# Revit family: RN 55035 Optipress-Therm-Übergang
name_source: partatom
category: Rohrformteile
units: mm (PartAtom-declared; Revit-internal decimal feet)

## family parameters
Arbeitsebenenbasiert = Nein
Beim Laden mit Abzugskörper schneiden = Nein
Bemaßung runder Anschluss = Durchmesser verwenden
Gemeinsam genutzt = Nein
Immer vertikal = Ja
Teiletyp = Verbindung

## types (23) — shared parameters
1.010.00.2 Blattnummer der Richtlinie = 29
1.010.00.3 Ausgabedatum (Monat) der Richtlinie = 201308
1.010.00.4 Herstellername = R. Nussbaum AG
1.010.00.5 Revisionsdatum der Datei = 20190521
1.010.00.6 Webadresse des Herstellers = http://www.nussbaum.ch
1.100.00.4 Produktbezeichnung = Versorgung
1.110.00.2 Index = 1
1.110.00.4 Produktbezeichnung = Optipress-Therm
1.960/3L.00.8 Link (URL) = https://www.nussbaum.ch
29.700.00.4 Produktname = Optipress-Therm-Übergang, mit Aussengewinde
29.700.00.5 Produktkennung = 2
29.700.00.6 Querschnittsform = 1
29.700.00.7 Nennweitensystem = DN
29.700.00.8 Nenndrucksystem = PN
29.710.02.4 Nenndruck = 16
29.710.02.5 max. zul. Überdruck [hPa] = 1600
29.710.02.7 max. zul. Dauer-Betriebsdruck [hPa] = 1600
29.710.02.9 max. zul. Dauer-Betriebstemperatur [°C] = 95
Connector Visibility = Nein
EnclosingSpace Visibility = Nein
R. Nussbaum AG 55035.30 de Visibility = Nein

## per-type parameters (varying)
- DN=60x65: 1.800.00.3 TGA-Nummer=01900100000000000000000000000000000000000000000022000000000000000023; 1.800.00.4 Kommentarfeld=55035.70, Optipress-Therm-Übergang, mit Aussengewinde, DN=60x65, L=108, R=2½; 1.810.00.3 Hersteller-Bestellnummer=55035.70; 1.810.00.4 DATANORM-Nummer=55035.70; 1.810.00.5 StLB-Nummer=255.624; 1.810.00.6 GTIN-Nummer=7612945679499; 29.710.02.10 Formstück-Gewicht [kg]=0.955; 29.710.02.3 Benennung=Optipress-Therm-Übergang, mit Aussengewinde, DN=60x65, L=108, R=2½; CONNECTOR0_DIAMETER_dX_0r=60 mm; CONNECTOR0_dX_01=43 mm  [stored 0.141076 ft]; CONNECTOR0_ref_dX=43 mm  [stored 0.141076 ft]; CONNECTOR1_DIAMETER_dX_0r=65 mm; CONNECTOR1_dX_00=81 mm; CONNECTOR1_dX_01=108 mm  [stored 0.354331 ft]; CONNECTOR1_ref_dX=81 mm; CONNENCTOR1_ref1_02=108 mm  [stored 0.354331 ft]; R. Nussbaum AG 55035.21 de Visibility=Nein; R. Nussbaum AG 55035.22 de Visibility=Nein; R. Nussbaum AG 55035.23 de Visibility=Nein; R. Nussbaum AG 55035.24 de Visibility=Nein; R. Nussbaum AG 55035.25 de Visibility=Nein; R. Nussbaum AG 55035.26 de Visibility=Nein; R. Nussbaum AG 55035.27 de Visibility=Nein; R. Nussbaum AG 55035.28 de Visibility=Nein; R. Nussbaum AG 55035.29 de Visibility=Nein; R. Nussbaum AG 55035.31 de Visibility=Nein; R. Nussbaum AG 55035.32 de Visibility=Nein; R. Nussbaum AG 55035.33 de Visibility=Nein; R. Nussbaum AG 55035.34 de Visibility=Nein; R. Nussbaum AG 55035.35 de Visibility=Nein; R. Nussbaum AG 55035.36 de Visibility=Nein; R. Nussbaum AG 55035.37 de Visibility=Nein; R. Nussbaum AG 55035.38 de Visibility=Nein; R. Nussbaum AG 55035.69 de Visibility=Nein; R. Nussbaum AG 55035.70 de Visibility=Ja; R. Nussbaum AG 55035.71 de Visibility=Nein; R. Nussbaum AG 55035.72 de Visibility=Nein; R. Nussbaum AG 55035.73 de Visibility=Nein
- DN=15x20: 1.800.00.3 TGA-Nummer=01900100000000000000000000000000000000000000000022000000000000000004; 1.800.00.4 Kommentarfeld=55035.24, Optipress-Therm-Übergang, mit Aussengewinde, DN=15x20, L=49, R=¾; 1.810.00.3 Hersteller-Bestellnummer=55035.24; 1.810.00.4 DATANORM-Nummer=55035.24; 1.810.00.5 StLB-Nummer=255.613; 1.810.00.6 GTIN-Nummer=7612945662378; 29.710.02.10 Formstück-Gewicht [kg]=0.059; 29.710.02.3 Benennung=Optipress-Therm-Übergang, mit Aussengewinde, DN=15x20, L=49, R=¾; CONNECTOR0_DIAMETER_dX_0r=15 mm  [stored 0.0492126 ft]; CONNECTOR0_dX_01=22 mm; CONNECTOR0_ref_dX=22 mm; CONNECTOR1_DIAMETER_dX_0r=20 mm; CONNECTOR1_dX_00=34 mm; CONNECTOR1_dX_01=49 mm; CONNECTOR1_ref_dX=34 mm; CONNENCTOR1_ref1_02=49 mm; R. Nussbaum AG 55035.21 de Visibility=Nein; R. Nussbaum AG 55035.22 de Visibility=Nein; R. Nussbaum AG 55035.23 de Visibility=Nein; R. Nussbaum AG 55035.24 de Visibility=Ja; R. Nussbaum AG 55035.25 de Visibility=Nein; R. Nussbaum AG 55035.26 de Visibility=Nein; R. Nussbaum AG 55035.27 de Visibility=Nein; R. Nussbaum AG 55035.28 de Visibility=Nein; R. Nussbaum AG 55035.29 de Visibility=Nein; R. Nussbaum AG 55035.31 de Visibility=Nein; R. Nussbaum AG 55035.32 de Visibility=Nein; R. Nussbaum AG 55035.33 de Visibility=Nein; R. Nussbaum AG 55035.34 de Visibility=Nein; R. Nussbaum AG 55035.35 de Visibility=Nein; R. Nussbaum AG 55035.36 de Visibility=Nein; R. Nussbaum AG 55035.37 de Visibility=Nein; R. Nussbaum AG 55035.38 de Visibility=Nein; R. Nussbaum AG 55035.69 de Visibility=Nein; R. Nussbaum AG 55035.70 de Visibility=Nein; R. Nussbaum AG 55035.71 de Visibility=Nein; R. Nussbaum AG 55035.72 de Visibility=Nein; R. Nussbaum AG 55035.73 de Visibility=Nein
- DN=100: 1.800.00.3 TGA-Nummer=01900100000000000000000000000000000000000000000022000000000000000021; 1.800.00.4 Kommentarfeld=55035.73, Optipress-Therm-Übergang, mit Aussengewinde, DN=100, L=134, R=4; 1.810.00.3 Hersteller-Bestellnummer=55035.73; 1.810.00.4 DATANORM-Nummer=55035.73; 1.810.00.5 StLB-Nummer=255.623; 1.810.00.6 GTIN-Nummer=7612945699244; 29.710.02.10 Formstück-Gewicht [kg]=1.553; 29.710.02.3 Benennung=Optipress-Therm-Übergang, mit Aussengewinde, DN=100, L=134, R=4; CONNECTOR0_DIAMETER_dX_0r=100 mm  [stored 0.328084 ft]; CONNECTOR0_dX_01=60 mm; CONNECTOR0_ref_dX=60 mm; CONNECTOR1_DIAMETER_dX_0r=100 mm  [stored 0.328084 ft]; CONNECTOR1_dX_00=98 mm; CONNECTOR1_dX_01=134 mm; CONNECTOR1_ref_dX=98 mm; CONNENCTOR1_ref1_02=134 mm; R. Nussbaum AG 55035.21 de Visibility=Nein; R. Nussbaum AG 55035.22 de Visibility=Nein; R. Nussbaum AG 55035.23 de Visibility=Nein; R. Nussbaum AG 55035.24 de Visibility=Nein; R. Nussbaum AG 55035.25 de Visibility=Nein; R. Nussbaum AG 55035.26 de Visibility=Nein; R. Nussbaum AG 55035.27 de Visibility=Nein; R. Nussbaum AG 55035.28 de Visibility=Nein; R. Nussbaum AG 55035.29 de Visibility=Nein; R. Nussbaum AG 55035.31 de Visibility=Nein; R. Nussbaum AG 55035.32 de Visibility=Nein; R. Nussbaum AG 55035.33 de Visibility=Nein; R. Nussbaum AG 55035.34 de Visibility=Nein; R. Nussbaum AG 55035.35 de Visibility=Nein; R. Nussbaum AG 55035.36 de Visibility=Nein; R. Nussbaum AG 55035.37 de Visibility=Nein; R. Nussbaum AG 55035.38 de Visibility=Nein; R. Nussbaum AG 55035.69 de Visibility=Nein; R. Nussbaum AG 55035.70 de Visibility=Nein; R. Nussbaum AG 55035.71 de Visibility=Nein; R. Nussbaum AG 55035.72 de Visibility=Nein; R. Nussbaum AG 55035.73 de Visibility=Ja
- DN=80: 1.800.00.3 TGA-Nummer=01900100000000000000000000000000000000000000000022000000000000000020; 1.800.00.4 Kommentarfeld=55035.72, Optipress-Therm-Übergang, mit Aussengewinde, DN=80, L=118, R=3; 1.810.00.3 Hersteller-Bestellnummer=55035.72; 1.810.00.4 DATANORM-Nummer=55035.72; 1.810.00.5 StLB-Nummer=255.622; 1.810.00.6 GTIN-Nummer=7612945699237; 29.710.02.10 Formstück-Gewicht [kg]=1.023; 29.710.02.3 Benennung=Optipress-Therm-Übergang, mit Aussengewinde, DN=80, L=118, R=3; CONNECTOR0_DIAMETER_dX_0r=80 mm; CONNECTOR0_dX_01=50 mm; CONNECTOR0_ref_dX=50 mm; CONNECTOR1_DIAMETER_dX_0r=80 mm; CONNECTOR1_dX_00=88 mm; CONNECTOR1_dX_01=118 mm; CONNECTOR1_ref_dX=88 mm; CONNENCTOR1_ref1_02=118 mm; R. Nussbaum AG 55035.21 de Visibility=Nein; R. Nussbaum AG 55035.22 de Visibility=Nein; R. Nussbaum AG 55035.23 de Visibility=Nein; R. Nussbaum AG 55035.24 de Visibility=Nein; R. Nussbaum AG 55035.25 de Visibility=Nein; R. Nussbaum AG 55035.26 de Visibility=Nein; R. Nussbaum AG 55035.27 de Visibility=Nein; R. Nussbaum AG 55035.28 de Visibility=Nein; R. Nussbaum AG 55035.29 de Visibility=Nein; R. Nussbaum AG 55035.31 de Visibility=Nein; R. Nussbaum AG 55035.32 de Visibility=Nein; R. Nussbaum AG 55035.33 de Visibility=Nein; R. Nussbaum AG 55035.34 de Visibility=Nein; R. Nussbaum AG 55035.35 de Visibility=Nein; R. Nussbaum AG 55035.36 de Visibility=Nein; R. Nussbaum AG 55035.37 de Visibility=Nein; R. Nussbaum AG 55035.38 de Visibility=Nein; R. Nussbaum AG 55035.69 de Visibility=Nein; R. Nussbaum AG 55035.70 de Visibility=Nein; R. Nussbaum AG 55035.71 de Visibility=Nein; R. Nussbaum AG 55035.72 de Visibility=Ja; R. Nussbaum AG 55035.73 de Visibility=Nein
- DN=65: 1.800.00.3 TGA-Nummer=01900100000000000000000000000000000000000000000022000000000000000019; 1.800.00.4 Kommentarfeld=55035.71, Optipress-Therm-Übergang, mit Aussengewinde, DN=65, L=114, R=2½; 1.810.00.3 Hersteller-Bestellnummer=55035.71; 1.810.00.4 DATANORM-Nummer=55035.71; 1.810.00.5 StLB-Nummer=255.621; 1.810.00.6 GTIN-Nummer=7612945681003; 29.710.02.10 Formstück-Gewicht [kg]=0.868; 29.710.02.3 Benennung=Optipress-Therm-Übergang, mit Aussengewinde, DN=65, L=114, R=2½; CONNECTOR0_DIAMETER_dX_0r=65 mm; CONNECTOR0_dX_01=50 mm; CONNECTOR0_ref_dX=50 mm; CONNECTOR1_DIAMETER_dX_0r=65 mm; CONNECTOR1_dX_00=87 mm; CONNECTOR1_dX_01=114 mm; CONNECTOR1_ref_dX=87 mm; CONNENCTOR1_ref1_02=114 mm; R. Nussbaum AG 55035.21 de Visibility=Nein; R. Nussbaum AG 55035.22 de Visibility=Nein; R. Nussbaum AG 55035.23 de Visibility=Nein; R. Nussbaum AG 55035.24 de Visibility=Nein; R. Nussbaum AG 55035.25 de Visibility=Nein; R. Nussbaum AG 55035.26 de Visibility=Nein; R. Nussbaum AG 55035.27 de Visibility=Nein; R. Nussbaum AG 55035.28 de Visibility=Nein; R. Nussbaum AG 55035.29 de Visibility=Nein; R. Nussbaum AG 55035.31 de Visibility=Nein; R. Nussbaum AG 55035.32 de Visibility=Nein; R. Nussbaum AG 55035.33 de Visibility=Nein; R. Nussbaum AG 55035.34 de Visibility=Nein; R. Nussbaum AG 55035.35 de Visibility=Nein; R. Nussbaum AG 55035.36 de Visibility=Nein; R. Nussbaum AG 55035.37 de Visibility=Nein; R. Nussbaum AG 55035.38 de Visibility=Nein; R. Nussbaum AG 55035.69 de Visibility=Nein; R. Nussbaum AG 55035.70 de Visibility=Nein; R. Nussbaum AG 55035.71 de Visibility=Ja; R. Nussbaum AG 55035.72 de Visibility=Nein; R. Nussbaum AG 55035.73 de Visibility=Nein
- DN=60x50: 1.800.00.3 TGA-Nummer=01900100000000000000000000000000000000000000000022000000000000000018; 1.800.00.4 Kommentarfeld=55035.69, Optipress-Therm-Übergang, mit Aussengewinde, DN=60x50, L=97, R=2; 1.810.00.3 Hersteller-Bestellnummer=55035.69; 1.810.00.4 DATANORM-Nummer=55035.69; 1.810.00.5 StLB-Nummer=255.624; 1.810.00.6 GTIN-Nummer=7612945679482; 29.710.02.10 Formstück-Gewicht [kg]=0.453; 29.710.02.3 Benennung=Optipress-Therm-Übergang, mit Aussengewinde, DN=60x50, L=97, R=2; CONNECTOR0_DIAMETER_dX_0r=60 mm; CONNECTOR0_dX_01=43 mm  [stored 0.141076 ft]; CONNECTOR0_ref_dX=43 mm  [stored 0.141076 ft]; CONNECTOR1_DIAMETER_dX_0r=50 mm; CONNECTOR1_dX_00=73 mm; CONNECTOR1_dX_01=97 mm; CONNECTOR1_ref_dX=73 mm; CONNENCTOR1_ref1_02=97 mm; R. Nussbaum AG 55035.21 de Visibility=Nein; R. Nussbaum AG 55035.22 de Visibility=Nein; R. Nussbaum AG 55035.23 de Visibility=Nein; R. Nussbaum AG 55035.24 de Visibility=Nein; R. Nussbaum AG 55035.25 de Visibility=Nein; R. Nussbaum AG 55035.26 de Visibility=Nein; R. Nussbaum AG 55035.27 de Visibility=Nein; R. Nussbaum AG 55035.28 de Visibility=Nein; R. Nussbaum AG 55035.29 de Visibility=Nein; R. Nussbaum AG 55035.31 de Visibility=Nein; R. Nussbaum AG 55035.32 de Visibility=Nein; R. Nussbaum AG 55035.33 de Visibility=Nein; R. Nussbaum AG 55035.34 de Visibility=Nein; R. Nussbaum AG 55035.35 de Visibility=Nein; R. Nussbaum AG 55035.36 de Visibility=Nein; R. Nussbaum AG 55035.37 de Visibility=Nein; R. Nussbaum AG 55035.38 de Visibility=Nein; R. Nussbaum AG 55035.69 de Visibility=Ja; R. Nussbaum AG 55035.70 de Visibility=Nein; R. Nussbaum AG 55035.71 de Visibility=Nein; R. Nussbaum AG 55035.72 de Visibility=Nein; R. Nussbaum AG 55035.73 de Visibility=Nein
- DN=25x15: 1.800.00.3 TGA-Nummer=01900100000000000000000000000000000000000000000022000000000000000017; 1.800.00.4 Kommentarfeld=55035.38, Optipress-Therm-Übergang, mit Aussengewinde, DN=25x15, L=50, R=½; 1.810.00.3 Hersteller-Bestellnummer=55035.38; 1.810.00.4 DATANORM-Nummer=55035.38; 1.810.00.5 StLB-Nummer=255.615; 1.810.00.6 GTIN-Nummer=7612945716378; 29.710.02.10 Formstück-Gewicht [kg]=0.088; 29.710.02.3 Benennung=Optipress-Therm-Übergang, mit Aussengewinde, DN=25x15, L=50, R=½; CONNECTOR0_DIAMETER_dX_0r=25 mm  [stored 0.082021 ft]; CONNECTOR0_dX_01=24 mm; CONNECTOR0_ref_dX=24 mm; CONNECTOR1_DIAMETER_dX_0r=15 mm  [stored 0.0492126 ft]; CONNECTOR1_dX_00=37 mm; CONNECTOR1_dX_01=50 mm; CONNECTOR1_ref_dX=37 mm; CONNENCTOR1_ref1_02=50 mm; R. Nussbaum AG 55035.21 de Visibility=Nein; R. Nussbaum AG 55035.22 de Visibility=Nein; R. Nussbaum AG 55035.23 de Visibility=Nein; R. Nussbaum AG 55035.24 de Visibility=Nein; R. Nussbaum AG 55035.25 de Visibility=Nein; R. Nussbaum AG 55035.26 de Visibility=Nein; R. Nussbaum AG 55035.27 de Visibility=Nein; R. Nussbaum AG 55035.28 de Visibility=Nein; R. Nussbaum AG 55035.29 de Visibility=Nein; R. Nussbaum AG 55035.31 de Visibility=Nein; R. Nussbaum AG 55035.32 de Visibility=Nein; R. Nussbaum AG 55035.33 de Visibility=Nein; R. Nussbaum AG 55035.34 de Visibility=Nein; R. Nussbaum AG 55035.35 de Visibility=Nein; R. Nussbaum AG 55035.36 de Visibility=Nein; R. Nussbaum AG 55035.37 de Visibility=Nein; R. Nussbaum AG 55035.38 de Visibility=Ja; R. Nussbaum AG 55035.69 de Visibility=Nein; R. Nussbaum AG 55035.70 de Visibility=Nein; R. Nussbaum AG 55035.71 de Visibility=Nein; R. Nussbaum AG 55035.72 de Visibility=Nein; R. Nussbaum AG 55035.73 de Visibility=Nein
- DN=40x32: 1.800.00.3 TGA-Nummer=01900100000000000000000000000000000000000000000022000000000000000016; 1.800.00.4 Kommentarfeld=55035.37, Optipress-Therm-Übergang, mit Aussengewinde, DN=40x32, L=77, R=1¼; 1.810.00.3 Hersteller-Bestellnummer=55035.37; 1.810.00.4 DATANORM-Nummer=55035.37; 1.810.00.5 StLB-Nummer=255.617; 1.810.00.6 GTIN-Nummer=7612945709004; 29.710.02.10 Formstück-Gewicht [kg]=0.334; 29.710.02.3 Benennung=Optipress-Therm-Übergang, mit Aussengewinde, DN=40x32, L=77, R=1¼; CONNECTOR0_DIAMETER_dX_0r=40 mm; CONNECTOR0_dX_01=36 mm; CONNECTOR0_ref_dX=36 mm; CONNECTOR1_DIAMETER_dX_0r=32 mm; CONNECTOR1_dX_00=58 mm; CONNECTOR1_dX_01=77 mm  [stored 0.252625 ft]; CONNECTOR1_ref_dX=58 mm; CONNENCTOR1_ref1_02=77 mm  [stored 0.252625 ft]; R. Nussbaum AG 55035.21 de Visibility=Nein; R. Nussbaum AG 55035.22 de Visibility=Nein; R. Nussbaum AG 55035.23 de Visibility=Nein; R. Nussbaum AG 55035.24 de Visibility=Nein; R. Nussbaum AG 55035.25 de Visibility=Nein; R. Nussbaum AG 55035.26 de Visibility=Nein; R. Nussbaum AG 55035.27 de Visibility=Nein; R. Nussbaum AG 55035.28 de Visibility=Nein; R. Nussbaum AG 55035.29 de Visibility=Nein; R. Nussbaum AG 55035.31 de Visibility=Nein; R. Nussbaum AG 55035.32 de Visibility=Nein; R. Nussbaum AG 55035.33 de Visibility=Nein; R. Nussbaum AG 55035.34 de Visibility=Nein; R. Nussbaum AG 55035.35 de Visibility=Nein; R. Nussbaum AG 55035.36 de Visibility=Nein; R. Nussbaum AG 55035.37 de Visibility=Ja; R. Nussbaum AG 55035.38 de Visibility=Nein; R. Nussbaum AG 55035.69 de Visibility=Nein; R. Nussbaum AG 55035.70 de Visibility=Nein; R. Nussbaum AG 55035.71 de Visibility=Nein; R. Nussbaum AG 55035.72 de Visibility=Nein; R. Nussbaum AG 55035.73 de Visibility=Nein
- DN=32x25: 1.800.00.3 TGA-Nummer=01900100000000000000000000000000000000000000000022000000000000000015; 1.800.00.4 Kommentarfeld=55035.36, Optipress-Therm-Übergang, mit Aussengewinde, DN=32x25, L=60, R=1; 1.810.00.3 Hersteller-Bestellnummer=55035.36; 1.810.00.4 DATANORM-Nummer=55035.36; 1.810.00.5 StLB-Nummer=255.616; 1.810.00.6 GTIN-Nummer=7612945708991; 29.710.02.10 Formstück-Gewicht [kg]=0.116; 29.710.02.3 Benennung=Optipress-Therm-Übergang, mit Aussengewinde, DN=32x25, L=60, R=1; CONNECTOR0_DIAMETER_dX_0r=32 mm; CONNECTOR0_dX_01=26 mm; CONNECTOR0_ref_dX=26 mm; CONNECTOR1_DIAMETER_dX_0r=25 mm  [stored 0.082021 ft]; CONNECTOR1_dX_00=43 mm  [stored 0.141076 ft]; CONNECTOR1_dX_01=60 mm; CONNECTOR1_ref_dX=43 mm  [stored 0.141076 ft]; CONNENCTOR1_ref1_02=60 mm; R. Nussbaum AG 55035.21 de Visibility=Nein; R. Nussbaum AG 55035.22 de Visibility=Nein; R. Nussbaum AG 55035.23 de Visibility=Nein; R. Nussbaum AG 55035.24 de Visibility=Nein; R. Nussbaum AG 55035.25 de Visibility=Nein; R. Nussbaum AG 55035.26 de Visibility=Nein; R. Nussbaum AG 55035.27 de Visibility=Nein; R. Nussbaum AG 55035.28 de Visibility=Nein; R. Nussbaum AG 55035.29 de Visibility=Nein; R. Nussbaum AG 55035.31 de Visibility=Nein; R. Nussbaum AG 55035.32 de Visibility=Nein; R. Nussbaum AG 55035.33 de Visibility=Nein; R. Nussbaum AG 55035.34 de Visibility=Nein; R. Nussbaum AG 55035.35 de Visibility=Nein; R. Nussbaum AG 55035.36 de Visibility=Ja; R. Nussbaum AG 55035.37 de Visibility=Nein; R. Nussbaum AG 55035.38 de Visibility=Nein; R. Nussbaum AG 55035.69 de Visibility=Nein; R. Nussbaum AG 55035.70 de Visibility=Nein; R. Nussbaum AG 55035.71 de Visibility=Nein; R. Nussbaum AG 55035.72 de Visibility=Nein; R. Nussbaum AG 55035.73 de Visibility=Nein
- DN=20x25: 1.800.00.3 TGA-Nummer=01900100000000000000000000000000000000000000000022000000000000000014; 1.800.00.4 Kommentarfeld=55035.35, Optipress-Therm-Übergang, mit Aussengewinde, DN=20x25, L=54, R=1; 1.810.00.3 Hersteller-Bestellnummer=55035.35; 1.810.00.4 DATANORM-Nummer=55035.35; 1.810.00.5 StLB-Nummer=255.614; 1.810.00.6 GTIN-Nummer=7612945708984; 29.710.02.10 Formstück-Gewicht [kg]=0.11; 29.710.02.3 Benennung=Optipress-Therm-Übergang, mit Aussengewinde, DN=20x25, L=54, R=1; CONNECTOR0_DIAMETER_dX_0r=20 mm; CONNECTOR0_dX_01=24 mm; CONNECTOR0_ref_dX=24 mm; CONNECTOR1_DIAMETER_dX_0r=25 mm  [stored 0.082021 ft]; CONNECTOR1_dX_00=37 mm; CONNECTOR1_dX_01=54 mm; CONNECTOR1_ref_dX=37 mm; CONNENCTOR1_ref1_02=54 mm; R. Nussbaum AG 55035.21 de Visibility=Nein; R. Nussbaum AG 55035.22 de Visibility=Nein; R. Nussbaum AG 55035.23 de Visibility=Nein; R. Nussbaum AG 55035.24 de Visibility=Nein; R. Nussbaum AG 55035.25 de Visibility=Nein; R. Nussbaum AG 55035.26 de Visibility=Nein; R. Nussbaum AG 55035.27 de Visibility=Nein; R. Nussbaum AG 55035.28 de Visibility=Nein; R. Nussbaum AG 55035.29 de Visibility=Nein; R. Nussbaum AG 55035.31 de Visibility=Nein; R. Nussbaum AG 55035.32 de Visibility=Nein; R. Nussbaum AG 55035.33 de Visibility=Nein; R. Nussbaum AG 55035.34 de Visibility=Nein; R. Nussbaum AG 55035.35 de Visibility=Ja; R. Nussbaum AG 55035.36 de Visibility=Nein; R. Nussbaum AG 55035.37 de Visibility=Nein; R. Nussbaum AG 55035.38 de Visibility=Nein; R. Nussbaum AG 55035.69 de Visibility=Nein; R. Nussbaum AG 55035.70 de Visibility=Nein; R. Nussbaum AG 55035.71 de Visibility=Nein; R. Nussbaum AG 55035.72 de Visibility=Nein; R. Nussbaum AG 55035.73 de Visibility=Nein
- DN=32x40: 1.800.00.3 TGA-Nummer=01900100000000000000000000000000000000000000000022000000000000000013; 1.800.00.4 Kommentarfeld=55035.34, Optipress-Therm-Übergang, mit Aussengewinde, DN=32x40, L=65, R=1½; 1.810.00.3 Hersteller-Bestellnummer=55035.34; 1.810.00.4 DATANORM-Nummer=55035.34; 1.810.00.5 StLB-Nummer=255.616; 1.810.00.6 GTIN-Nummer=7612945685674; 29.710.02.10 Formstück-Gewicht [kg]=0.241; 29.710.02.3 Benennung=Optipress-Therm-Übergang, mit Aussengewinde, DN=32x40, L=65, R=1½; CONNECTOR0_DIAMETER_dX_0r=32 mm; CONNECTOR0_dX_01=26 mm; CONNECTOR0_ref_dX=26 mm; CONNECTOR1_DIAMETER_dX_0r=40 mm; CONNECTOR1_dX_00=46 mm; CONNECTOR1_dX_01=65 mm; CONNECTOR1_ref_dX=46 mm; CONNENCTOR1_ref1_02=65 mm; Hersteller=R. Nussbaum AG; Modell=55035.34; R. Nussbaum AG 55035.21 de Visibility=Nein; R. Nussbaum AG 55035.22 de Visibility=Nein; R. Nussbaum AG 55035.23 de Visibility=Nein; R. Nussbaum AG 55035.24 de Visibility=Nein; R. Nussbaum AG 55035.25 de Visibility=Nein; R. Nussbaum AG 55035.26 de Visibility=Nein; R. Nussbaum AG 55035.27 de Visibility=Nein; R. Nussbaum AG 55035.28 de Visibility=Nein; R. Nussbaum AG 55035.29 de Visibility=Nein; R. Nussbaum AG 55035.31 de Visibility=Nein; R. Nussbaum AG 55035.32 de Visibility=Nein; R. Nussbaum AG 55035.33 de Visibility=Nein; R. Nussbaum AG 55035.34 de Visibility=Ja; R. Nussbaum AG 55035.35 de Visibility=Nein; R. Nussbaum AG 55035.36 de Visibility=Nein; R. Nussbaum AG 55035.37 de Visibility=Nein; R. Nussbaum AG 55035.38 de Visibility=Nein; R. Nussbaum AG 55035.69 de Visibility=Nein; R. Nussbaum AG 55035.70 de Visibility=Nein; R. Nussbaum AG 55035.71 de Visibility=Nein; R. Nussbaum AG 55035.72 de Visibility=Nein; R. Nussbaum AG 55035.73 de Visibility=Nein; Typenkommentare=Optipress-Therm-Übergang DN=32x40
- DN=25x32: 1.800.00.3 TGA-Nummer=01900100000000000000000000000000000000000000000022000000000000000012; 1.800.00.4 Kommentarfeld=55035.33, Optipress-Therm-Übergang, mit Aussengewinde, DN=25x32, L=62, R=1¼; 1.810.00.3 Hersteller-Bestellnummer=55035.33; 1.810.00.4 DATANORM-Nummer=55035.33; 1.810.00.5 StLB-Nummer=255.615; 1.810.00.6 GTIN-Nummer=7612945685667; 29.710.02.10 Formstück-Gewicht [kg]=0.215; 29.710.02.3 Benennung=Optipress-Therm-Übergang, mit Aussengewinde, DN=25x32, L=62, R=1¼; CONNECTOR0_DIAMETER_dX_0r=25 mm  [stored 0.082021 ft]; CONNECTOR0_dX_01=24 mm; CONNECTOR0_ref_dX=24 mm; CONNECTOR1_DIAMETER_dX_0r=32 mm; CONNECTOR1_dX_00=43 mm  [stored 0.141076 ft]; CONNECTOR1_dX_01=62 mm; CONNECTOR1_ref_dX=43 mm  [stored 0.141076 ft]; CONNENCTOR1_ref1_02=62 mm; R. Nussbaum AG 55035.21 de Visibility=Nein; R. Nussbaum AG 55035.22 de Visibility=Nein; R. Nussbaum AG 55035.23 de Visibility=Nein; R. Nussbaum AG 55035.24 de Visibility=Nein; R. Nussbaum AG 55035.25 de Visibility=Nein; R. Nussbaum AG 55035.26 de Visibility=Nein; R. Nussbaum AG 55035.27 de Visibility=Nein; R. Nussbaum AG 55035.28 de Visibility=Nein; R. Nussbaum AG 55035.29 de Visibility=Nein; R. Nussbaum AG 55035.31 de Visibility=Nein; R. Nussbaum AG 55035.32 de Visibility=Nein; R. Nussbaum AG 55035.33 de Visibility=Ja; R. Nussbaum AG 55035.34 de Visibility=Nein; R. Nussbaum AG 55035.35 de Visibility=Nein; R. Nussbaum AG 55035.36 de Visibility=Nein; R. Nussbaum AG 55035.37 de Visibility=Nein; R. Nussbaum AG 55035.38 de Visibility=Nein; R. Nussbaum AG 55035.69 de Visibility=Nein; R. Nussbaum AG 55035.70 de Visibility=Nein; R. Nussbaum AG 55035.71 de Visibility=Nein; R. Nussbaum AG 55035.72 de Visibility=Nein; R. Nussbaum AG 55035.73 de Visibility=Nein
- DN=25x20: 1.800.00.3 TGA-Nummer=01900100000000000000000000000000000000000000000022000000000000000011; 1.800.00.4 Kommentarfeld=55035.32, Optipress-Therm-Übergang, mit Aussengewinde, DN=25x20, L=52, R=¾; 1.810.00.3 Hersteller-Bestellnummer=55035.32; 1.810.00.4 DATANORM-Nummer=55035.32; 1.810.00.5 StLB-Nummer=255.615; 1.810.00.6 GTIN-Nummer=7612945685650; 29.710.02.10 Formstück-Gewicht [kg]=0.085; 29.710.02.3 Benennung=Optipress-Therm-Übergang, mit Aussengewinde, DN=25x20, L=52, R=¾; CONNECTOR0_DIAMETER_dX_0r=25 mm  [stored 0.082021 ft]; CONNECTOR0_dX_01=24 mm; CONNECTOR0_ref_dX=24 mm; CONNECTOR1_DIAMETER_dX_0r=20 mm; CONNECTOR1_dX_00=37 mm; CONNECTOR1_dX_01=52 mm  [stored 0.170604 ft]; CONNECTOR1_ref_dX=37 mm; CONNENCTOR1_ref1_02=52 mm  [stored 0.170604 ft]; R. Nussbaum AG 55035.21 de Visibility=Nein; R. Nussbaum AG 55035.22 de Visibility=Nein; R. Nussbaum AG 55035.23 de Visibility=Nein; R. Nussbaum AG 55035.24 de Visibility=Nein; R. Nussbaum AG 55035.25 de Visibility=Nein; R. Nussbaum AG 55035.26 de Visibility=Nein; R. Nussbaum AG 55035.27 de Visibility=Nein; R. Nussbaum AG 55035.28 de Visibility=Nein; R. Nussbaum AG 55035.29 de Visibility=Nein; R. Nussbaum AG 55035.31 de Visibility=Nein; R. Nussbaum AG 55035.32 de Visibility=Ja; R. Nussbaum AG 55035.33 de Visibility=Nein; R. Nussbaum AG 55035.34 de Visibility=Nein; R. Nussbaum AG 55035.35 de Visibility=Nein; R. Nussbaum AG 55035.36 de Visibility=Nein; R. Nussbaum AG 55035.37 de Visibility=Nein; R. Nussbaum AG 55035.38 de Visibility=Nein; R. Nussbaum AG 55035.69 de Visibility=Nein; R. Nussbaum AG 55035.70 de Visibility=Nein; R. Nussbaum AG 55035.71 de Visibility=Nein; R. Nussbaum AG 55035.72 de Visibility=Nein; R. Nussbaum AG 55035.73 de Visibility=Nein
- DN=20x15: 1.800.00.3 TGA-Nummer=01900100000000000000000000000000000000000000000022000000000000000010; 1.800.00.4 Kommentarfeld=55035.31, Optipress-Therm-Übergang, mit Aussengewinde, DN=20x15, L=48, R=½; 1.810.00.3 Hersteller-Bestellnummer=55035.31; 1.810.00.4 DATANORM-Nummer=55035.31; 1.810.00.5 StLB-Nummer=255.614; 1.810.00.6 GTIN-Nummer=7612945685643; 29.710.02.10 Formstück-Gewicht [kg]=0.062; 29.710.02.3 Benennung=Optipress-Therm-Übergang, mit Aussengewinde, DN=20x15, L=48, R=½; CONNECTOR0_DIAMETER_dX_0r=20 mm; CONNECTOR0_dX_01=24 mm; CONNECTOR0_ref_dX=24 mm; CONNECTOR1_DIAMETER_dX_0r=15 mm  [stored 0.0492126 ft]; CONNECTOR1_dX_00=35 mm; CONNECTOR1_dX_01=48 mm; CONNECTOR1_ref_dX=35 mm; CONNENCTOR1_ref1_02=48 mm; Hersteller=R. Nussbaum AG; Modell=55035.31; R. Nussbaum AG 55035.21 de Visibility=Nein; R. Nussbaum AG 55035.22 de Visibility=Nein; R. Nussbaum AG 55035.23 de Visibility=Nein; R. Nussbaum AG 55035.24 de Visibility=Nein; R. Nussbaum AG 55035.25 de Visibility=Nein; R. Nussbaum AG 55035.26 de Visibility=Nein; R. Nussbaum AG 55035.27 de Visibility=Nein; R. Nussbaum AG 55035.28 de Visibility=Nein; R. Nussbaum AG 55035.29 de Visibility=Nein; R. Nussbaum AG 55035.31 de Visibility=Ja; R. Nussbaum AG 55035.32 de Visibility=Nein; R. Nussbaum AG 55035.33 de Visibility=Nein; R. Nussbaum AG 55035.34 de Visibility=Nein; R. Nussbaum AG 55035.35 de Visibility=Nein; R. Nussbaum AG 55035.36 de Visibility=Nein; R. Nussbaum AG 55035.37 de Visibility=Nein; R. Nussbaum AG 55035.38 de Visibility=Nein; R. Nussbaum AG 55035.69 de Visibility=Nein; R. Nussbaum AG 55035.70 de Visibility=Nein; R. Nussbaum AG 55035.71 de Visibility=Nein; R. Nussbaum AG 55035.72 de Visibility=Nein; R. Nussbaum AG 55035.73 de Visibility=Nein; Typenkommentare=Optipress-Therm-Übergang DN=20x15
- DN=50: 1.800.00.3 TGA-Nummer=01900100000000000000000000000000000000000000000022000000000000000009; 1.800.00.4 Kommentarfeld=55035.29, Optipress-Therm-Übergang, mit Aussengewinde, DN=50, L=82, R=2; 1.810.00.3 Hersteller-Bestellnummer=55035.29; 1.810.00.4 DATANORM-Nummer=55035.29; 1.810.00.5 StLB-Nummer=255.618; 1.810.00.6 GTIN-Nummer=7612945662477; 29.710.02.10 Formstück-Gewicht [kg]=0.457; 29.710.02.3 Benennung=Optipress-Therm-Übergang, mit Aussengewinde, DN=50, L=82, R=2; CONNECTOR0_DIAMETER_dX_0r=50 mm; CONNECTOR0_dX_01=40 mm; CONNECTOR0_ref_dX=40 mm; CONNECTOR1_DIAMETER_dX_0r=50 mm; CONNECTOR1_dX_00=58 mm; CONNECTOR1_dX_01=82 mm; CONNECTOR1_ref_dX=58 mm; CONNENCTOR1_ref1_02=82 mm; Hersteller=R. Nussbaum AG; Modell=55035.29; R. Nussbaum AG 55035.21 de Visibility=Nein; R. Nussbaum AG 55035.22 de Visibility=Nein; R. Nussbaum AG 55035.23 de Visibility=Nein; R. Nussbaum AG 55035.24 de Visibility=Nein; R. Nussbaum AG 55035.25 de Visibility=Nein; R. Nussbaum AG 55035.26 de Visibility=Nein; R. Nussbaum AG 55035.27 de Visibility=Nein; R. Nussbaum AG 55035.28 de Visibility=Nein; R. Nussbaum AG 55035.29 de Visibility=Ja; R. Nussbaum AG 55035.31 de Visibility=Nein; R. Nussbaum AG 55035.32 de Visibility=Nein; R. Nussbaum AG 55035.33 de Visibility=Nein; R. Nussbaum AG 55035.34 de Visibility=Nein; R. Nussbaum AG 55035.35 de Visibility=Nein; R. Nussbaum AG 55035.36 de Visibility=Nein; R. Nussbaum AG 55035.37 de Visibility=Nein; R. Nussbaum AG 55035.38 de Visibility=Nein; R. Nussbaum AG 55035.69 de Visibility=Nein; R. Nussbaum AG 55035.70 de Visibility=Nein; R. Nussbaum AG 55035.71 de Visibility=Nein; R. Nussbaum AG 55035.72 de Visibility=Nein; R. Nussbaum AG 55035.73 de Visibility=Nein; Typenkommentare=Optipress-Therm-Übergang DN=50
- DN=40: 1.800.00.3 TGA-Nummer=01900100000000000000000000000000000000000000000022000000000000000008; 1.800.00.4 Kommentarfeld=55035.28, Optipress-Therm-Übergang, mit Aussengewinde, DN=40, L=72, R=1½; 1.810.00.3 Hersteller-Bestellnummer=55035.28; 1.810.00.4 DATANORM-Nummer=55035.28; 1.810.00.5 StLB-Nummer=255.617; 1.810.00.6 GTIN-Nummer=7612945662453; 29.710.02.10 Formstück-Gewicht [kg]=0.294; 29.710.02.3 Benennung=Optipress-Therm-Übergang, mit Aussengewinde, DN=40, L=72, R=1½; CONNECTOR0_DIAMETER_dX_0r=40 mm; CONNECTOR0_dX_01=36 mm; CONNECTOR0_ref_dX=36 mm; CONNECTOR1_DIAMETER_dX_0r=40 mm; CONNECTOR1_dX_00=53 mm; CONNECTOR1_dX_01=72 mm; CONNECTOR1_ref_dX=53 mm; CONNENCTOR1_ref1_02=72 mm; Hersteller=R. Nussbaum AG; Modell=55035.28; R. Nussbaum AG 55035.21 de Visibility=Nein; R. Nussbaum AG 55035.22 de Visibility=Nein; R. Nussbaum AG 55035.23 de Visibility=Nein; R. Nussbaum AG 55035.24 de Visibility=Nein; R. Nussbaum AG 55035.25 de Visibility=Nein; R. Nussbaum AG 55035.26 de Visibility=Nein; R. Nussbaum AG 55035.27 de Visibility=Nein; R. Nussbaum AG 55035.28 de Visibility=Ja; R. Nussbaum AG 55035.29 de Visibility=Nein; R. Nussbaum AG 55035.31 de Visibility=Nein; R. Nussbaum AG 55035.32 de Visibility=Nein; R. Nussbaum AG 55035.33 de Visibility=Nein; R. Nussbaum AG 55035.34 de Visibility=Nein; R. Nussbaum AG 55035.35 de Visibility=Nein; R. Nussbaum AG 55035.36 de Visibility=Nein; R. Nussbaum AG 55035.37 de Visibility=Nein; R. Nussbaum AG 55035.38 de Visibility=Nein; R. Nussbaum AG 55035.69 de Visibility=Nein; R. Nussbaum AG 55035.70 de Visibility=Nein; R. Nussbaum AG 55035.71 de Visibility=Nein; R. Nussbaum AG 55035.72 de Visibility=Nein; R. Nussbaum AG 55035.73 de Visibility=Nein; Typenkommentare=Optipress-Therm-Übergang DN=40
- DN=32: 1.800.00.3 TGA-Nummer=01900100000000000000000000000000000000000000000022000000000000000007; 1.800.00.4 Kommentarfeld=55035.27, Optipress-Therm-Übergang, mit Aussengewinde, DN=32, L=62, R=1¼; 1.810.00.3 Hersteller-Bestellnummer=55035.27; 1.810.00.4 DATANORM-Nummer=55035.27; 1.810.00.5 StLB-Nummer=255.616; 1.810.00.6 GTIN-Nummer=7612945662439; 29.710.02.10 Formstück-Gewicht [kg]=0.213; 29.710.02.3 Benennung=Optipress-Therm-Übergang, mit Aussengewinde, DN=32, L=62, R=1¼; CONNECTOR0_DIAMETER_dX_0r=32 mm; CONNECTOR0_dX_01=26 mm; CONNECTOR0_ref_dX=26 mm; CONNECTOR1_DIAMETER_dX_0r=32 mm; CONNECTOR1_dX_00=43 mm  [stored 0.141076 ft]; CONNECTOR1_dX_01=62 mm; CONNECTOR1_ref_dX=43 mm  [stored 0.141076 ft]; CONNENCTOR1_ref1_02=62 mm; Hersteller=R. Nussbaum AG; Modell=55035.27; R. Nussbaum AG 55035.21 de Visibility=Nein; R. Nussbaum AG 55035.22 de Visibility=Nein; R. Nussbaum AG 55035.23 de Visibility=Nein; R. Nussbaum AG 55035.24 de Visibility=Nein; R. Nussbaum AG 55035.25 de Visibility=Nein; R. Nussbaum AG 55035.26 de Visibility=Nein; R. Nussbaum AG 55035.27 de Visibility=Ja; R. Nussbaum AG 55035.28 de Visibility=Nein; R. Nussbaum AG 55035.29 de Visibility=Nein; R. Nussbaum AG 55035.31 de Visibility=Nein; R. Nussbaum AG 55035.32 de Visibility=Nein; R. Nussbaum AG 55035.33 de Visibility=Nein; R. Nussbaum AG 55035.34 de Visibility=Nein; R. Nussbaum AG 55035.35 de Visibility=Nein; R. Nussbaum AG 55035.36 de Visibility=Nein; R. Nussbaum AG 55035.37 de Visibility=Nein; R. Nussbaum AG 55035.38 de Visibility=Nein; R. Nussbaum AG 55035.69 de Visibility=Nein; R. Nussbaum AG 55035.70 de Visibility=Nein; R. Nussbaum AG 55035.71 de Visibility=Nein; R. Nussbaum AG 55035.72 de Visibility=Nein; R. Nussbaum AG 55035.73 de Visibility=Nein; Typenkommentare=Optipress-Therm-Übergang DN=32
- DN=25: 1.800.00.3 TGA-Nummer=01900100000000000000000000000000000000000000000022000000000000000006; 1.800.00.4 Kommentarfeld=55035.26, Optipress-Therm-Übergang, mit Aussengewinde, DN=25, L=54, R=1; 1.810.00.3 Hersteller-Bestellnummer=55035.26; 1.810.00.4 DATANORM-Nummer=55035.26; 1.810.00.5 StLB-Nummer=255.615; 1.810.00.6 GTIN-Nummer=7612945662415; 29.710.02.10 Formstück-Gewicht [kg]=0.101; 29.710.02.3 Benennung=Optipress-Therm-Übergang, mit Aussengewinde, DN=25, L=54, R=1; CONNECTOR0_DIAMETER_dX_0r=25 mm  [stored 0.082021 ft]; CONNECTOR0_dX_01=24 mm; CONNECTOR0_ref_dX=24 mm; CONNECTOR1_DIAMETER_dX_0r=25 mm  [stored 0.082021 ft]; CONNECTOR1_dX_00=37 mm; CONNECTOR1_dX_01=54 mm; CONNECTOR1_ref_dX=37 mm; CONNENCTOR1_ref1_02=54 mm; Hersteller=R. Nussbaum AG; Modell=55035.26; R. Nussbaum AG 55035.21 de Visibility=Nein; R. Nussbaum AG 55035.22 de Visibility=Nein; R. Nussbaum AG 55035.23 de Visibility=Nein; R. Nussbaum AG 55035.24 de Visibility=Nein; R. Nussbaum AG 55035.25 de Visibility=Nein; R. Nussbaum AG 55035.26 de Visibility=Ja; R. Nussbaum AG 55035.27 de Visibility=Nein; R. Nussbaum AG 55035.28 de Visibility=Nein; R. Nussbaum AG 55035.29 de Visibility=Nein; R. Nussbaum AG 55035.31 de Visibility=Nein; R. Nussbaum AG 55035.32 de Visibility=Nein; R. Nussbaum AG 55035.33 de Visibility=Nein; R. Nussbaum AG 55035.34 de Visibility=Nein; R. Nussbaum AG 55035.35 de Visibility=Nein; R. Nussbaum AG 55035.36 de Visibility=Nein; R. Nussbaum AG 55035.37 de Visibility=Nein; R. Nussbaum AG 55035.38 de Visibility=Nein; R. Nussbaum AG 55035.69 de Visibility=Nein; R. Nussbaum AG 55035.70 de Visibility=Nein; R. Nussbaum AG 55035.71 de Visibility=Nein; R. Nussbaum AG 55035.72 de Visibility=Nein; R. Nussbaum AG 55035.73 de Visibility=Nein; Typenkommentare=Optipress-Therm-Übergang DN=25
- DN=20: 1.800.00.3 TGA-Nummer=01900100000000000000000000000000000000000000000022000000000000000005; 1.800.00.4 Kommentarfeld=55035.25, Optipress-Therm-Übergang, mit Aussengewinde, DN=20, L=49, R=¾; 1.810.00.3 Hersteller-Bestellnummer=55035.25; 1.810.00.4 DATANORM-Nummer=55035.25; 1.810.00.5 StLB-Nummer=255.614; 1.810.00.6 GTIN-Nummer=7612945662392; 29.710.02.10 Formstück-Gewicht [kg]=0.061; 29.710.02.3 Benennung=Optipress-Therm-Übergang, mit Aussengewinde, DN=20, L=49, R=¾; CONNECTOR0_DIAMETER_dX_0r=20 mm; CONNECTOR0_dX_01=24 mm; CONNECTOR0_ref_dX=24 mm; CONNECTOR1_DIAMETER_dX_0r=20 mm; CONNECTOR1_dX_00=34 mm; CONNECTOR1_dX_01=49 mm; CONNECTOR1_ref_dX=34 mm; CONNENCTOR1_ref1_02=49 mm; Hersteller=R. Nussbaum AG; Modell=55035.25; R. Nussbaum AG 55035.21 de Visibility=Nein; R. Nussbaum AG 55035.22 de Visibility=Nein; R. Nussbaum AG 55035.23 de Visibility=Nein; R. Nussbaum AG 55035.24 de Visibility=Nein; R. Nussbaum AG 55035.25 de Visibility=Ja; R. Nussbaum AG 55035.26 de Visibility=Nein; R. Nussbaum AG 55035.27 de Visibility=Nein; R. Nussbaum AG 55035.28 de Visibility=Nein; R. Nussbaum AG 55035.29 de Visibility=Nein; R. Nussbaum AG 55035.31 de Visibility=Nein; R. Nussbaum AG 55035.32 de Visibility=Nein; R. Nussbaum AG 55035.33 de Visibility=Nein; R. Nussbaum AG 55035.34 de Visibility=Nein; R. Nussbaum AG 55035.35 de Visibility=Nein; R. Nussbaum AG 55035.36 de Visibility=Nein; R. Nussbaum AG 55035.37 de Visibility=Nein; R. Nussbaum AG 55035.38 de Visibility=Nein; R. Nussbaum AG 55035.69 de Visibility=Nein; R. Nussbaum AG 55035.70 de Visibility=Nein; R. Nussbaum AG 55035.71 de Visibility=Nein; R. Nussbaum AG 55035.72 de Visibility=Nein; R. Nussbaum AG 55035.73 de Visibility=Nein; Typenkommentare=Optipress-Therm-Übergang DN=20
- DN=15: 1.800.00.3 TGA-Nummer=01900100000000000000000000000000000000000000000022000000000000000003; 1.800.00.4 Kommentarfeld=55035.23, Optipress-Therm-Übergang, mit Aussengewinde, DN=15, L=46, R=½; 1.810.00.3 Hersteller-Bestellnummer=55035.23; 1.810.00.4 DATANORM-Nummer=55035.23; 1.810.00.5 StLB-Nummer=255.613; 1.810.00.6 GTIN-Nummer=7612945662354; 29.710.02.10 Formstück-Gewicht [kg]=0.048; 29.710.02.3 Benennung=Optipress-Therm-Übergang, mit Aussengewinde, DN=15, L=46, R=½; CONNECTOR0_DIAMETER_dX_0r=15 mm  [stored 0.0492126 ft]; CONNECTOR0_dX_01=22 mm; CONNECTOR0_ref_dX=22 mm; CONNECTOR1_DIAMETER_dX_0r=15 mm  [stored 0.0492126 ft]; CONNECTOR1_dX_00=33 mm  [stored 0.108268 ft]; CONNECTOR1_dX_01=46 mm; CONNECTOR1_ref_dX=33 mm  [stored 0.108268 ft]; CONNENCTOR1_ref1_02=46 mm; Hersteller=R. Nussbaum AG; Modell=55035.23; R. Nussbaum AG 55035.21 de Visibility=Nein; R. Nussbaum AG 55035.22 de Visibility=Nein; R. Nussbaum AG 55035.23 de Visibility=Ja; R. Nussbaum AG 55035.24 de Visibility=Nein; R. Nussbaum AG 55035.25 de Visibility=Nein; R. Nussbaum AG 55035.26 de Visibility=Nein; R. Nussbaum AG 55035.27 de Visibility=Nein; R. Nussbaum AG 55035.28 de Visibility=Nein; R. Nussbaum AG 55035.29 de Visibility=Nein; R. Nussbaum AG 55035.31 de Visibility=Nein; R. Nussbaum AG 55035.32 de Visibility=Nein; R. Nussbaum AG 55035.33 de Visibility=Nein; R. Nussbaum AG 55035.34 de Visibility=Nein; R. Nussbaum AG 55035.35 de Visibility=Nein; R. Nussbaum AG 55035.36 de Visibility=Nein; R. Nussbaum AG 55035.37 de Visibility=Nein; R. Nussbaum AG 55035.38 de Visibility=Nein; R. Nussbaum AG 55035.69 de Visibility=Nein; R. Nussbaum AG 55035.70 de Visibility=Nein; R. Nussbaum AG 55035.71 de Visibility=Nein; R. Nussbaum AG 55035.72 de Visibility=Nein; R. Nussbaum AG 55035.73 de Visibility=Nein; Typenkommentare=Optipress-Therm-Übergang DN=15
- DN=12x15: 1.800.00.3 TGA-Nummer=01900100000000000000000000000000000000000000000022000000000000000002; 1.800.00.4 Kommentarfeld=55035.22, Optipress-Therm-Übergang, mit Aussengewinde, DN=12x15, L=46, R=½; 1.810.00.3 Hersteller-Bestellnummer=55035.22; 1.810.00.4 DATANORM-Nummer=55035.22; 1.810.00.5 StLB-Nummer=255.612; 1.810.00.6 GTIN-Nummer=7612945662330; 29.710.02.10 Formstück-Gewicht [kg]=0.045; 29.710.02.3 Benennung=Optipress-Therm-Übergang, mit Aussengewinde, DN=12x15, L=46, R=½; CONNECTOR0_DIAMETER_dX_0r=12 mm  [stored 0.0393701 ft]; CONNECTOR0_dX_01=22 mm; CONNECTOR0_ref_dX=22 mm; CONNECTOR1_DIAMETER_dX_0r=15 mm  [stored 0.0492126 ft]; CONNECTOR1_dX_00=33 mm  [stored 0.108268 ft]; CONNECTOR1_dX_01=46 mm; CONNECTOR1_ref_dX=33 mm  [stored 0.108268 ft]; CONNENCTOR1_ref1_02=46 mm; Hersteller=R. Nussbaum AG; Modell=55035.22; R. Nussbaum AG 55035.21 de Visibility=Nein; R. Nussbaum AG 55035.22 de Visibility=Ja; R. Nussbaum AG 55035.23 de Visibility=Nein; R. Nussbaum AG 55035.24 de Visibility=Nein; R. Nussbaum AG 55035.25 de Visibility=Nein; R. Nussbaum AG 55035.26 de Visibility=Nein; R. Nussbaum AG 55035.27 de Visibility=Nein; R. Nussbaum AG 55035.28 de Visibility=Nein; R. Nussbaum AG 55035.29 de Visibility=Nein; R. Nussbaum AG 55035.31 de Visibility=Nein; R. Nussbaum AG 55035.32 de Visibility=Nein; R. Nussbaum AG 55035.33 de Visibility=Nein; R. Nussbaum AG 55035.34 de Visibility=Nein; R. Nussbaum AG 55035.35 de Visibility=Nein; R. Nussbaum AG 55035.36 de Visibility=Nein; R. Nussbaum AG 55035.37 de Visibility=Nein; R. Nussbaum AG 55035.38 de Visibility=Nein; R. Nussbaum AG 55035.69 de Visibility=Nein; R. Nussbaum AG 55035.70 de Visibility=Nein; R. Nussbaum AG 55035.71 de Visibility=Nein; R. Nussbaum AG 55035.72 de Visibility=Nein; R. Nussbaum AG 55035.73 de Visibility=Nein; Typenkommentare=Optipress-Therm-Übergang DN=12x15
- DN=15x12: 1.800.00.3 TGA-Nummer=01900100000000000000000000000000000000000000000022000000000000000001; 1.800.00.4 Kommentarfeld=55035.21, Optipress-Therm-Übergang, mit Aussengewinde, DN=15x12, L=42, R=3/8; 1.810.00.3 Hersteller-Bestellnummer=55035.21; 1.810.00.4 DATANORM-Nummer=55035.21; 1.810.00.5 StLB-Nummer=255.612; 1.810.00.6 GTIN-Nummer=7612945662323; 29.710.02.10 Formstück-Gewicht [kg]=0.03; 29.710.02.3 Benennung=Optipress-Therm-Übergang, mit Aussengewinde, DN=15x12, L=42, R=3/8; CONNECTOR0_DIAMETER_dX_0r=15 mm  [stored 0.0492126 ft]; CONNECTOR0_dX_01=22 mm; CONNECTOR0_ref_dX=22 mm; CONNECTOR1_DIAMETER_dX_0r=12 mm  [stored 0.0393701 ft]; CONNECTOR1_dX_00=32 mm; CONNECTOR1_dX_01=42 mm  [stored 0.137795 ft]; CONNECTOR1_ref_dX=32 mm; CONNENCTOR1_ref1_02=42 mm  [stored 0.137795 ft]; Hersteller=R. Nussbaum AG; Modell=55035.21; R. Nussbaum AG 55035.21 de Visibility=Ja; R. Nussbaum AG 55035.22 de Visibility=Nein; R. Nussbaum AG 55035.23 de Visibility=Nein; R. Nussbaum AG 55035.24 de Visibility=Nein; R. Nussbaum AG 55035.25 de Visibility=Nein; R. Nussbaum AG 55035.26 de Visibility=Nein; R. Nussbaum AG 55035.27 de Visibility=Nein; R. Nussbaum AG 55035.28 de Visibility=Nein; R. Nussbaum AG 55035.29 de Visibility=Nein; R. Nussbaum AG 55035.31 de Visibility=Nein; R. Nussbaum AG 55035.32 de Visibility=Nein; R. Nussbaum AG 55035.33 de Visibility=Nein; R. Nussbaum AG 55035.34 de Visibility=Nein; R. Nussbaum AG 55035.35 de Visibility=Nein; R. Nussbaum AG 55035.36 de Visibility=Nein; R. Nussbaum AG 55035.37 de Visibility=Nein; R. Nussbaum AG 55035.38 de Visibility=Nein; R. Nussbaum AG 55035.69 de Visibility=Nein; R. Nussbaum AG 55035.70 de Visibility=Nein; R. Nussbaum AG 55035.71 de Visibility=Nein; R. Nussbaum AG 55035.72 de Visibility=Nein; R. Nussbaum AG 55035.73 de Visibility=Nein; Typenkommentare=Optipress-Therm-Übergang DN=15x12
- DN=15x1: 1.800.00.3 TGA-Nummer=01900100000000000000000000000000000000000000000022000000000000000004; 1.800.00.4 Kommentarfeld=55035.24, Optipress-Therm-Übergang, mit Aussengewinde, DN=15x20, L=49, R=¾; 1.810.00.3 Hersteller-Bestellnummer=55035.24; 1.810.00.4 DATANORM-Nummer=55035.24; 1.810.00.5 StLB-Nummer=255.613; 1.810.00.6 GTIN-Nummer=7612945662378; 29.710.02.10 Formstück-Gewicht [kg]=0.059; 29.710.02.3 Benennung=Optipress-Therm-Übergang, mit Aussengewinde, DN=15x20, L=49, R=¾; CONNECTOR0_DIAMETER_dX_0r=15 mm  [stored 0.0492126 ft]; CONNECTOR0_dX_01=22 mm; CONNECTOR0_ref_dX=22 mm; CONNECTOR1_DIAMETER_dX_0r=20 mm; CONNECTOR1_dX_00=34 mm; CONNECTOR1_dX_01=49 mm; CONNECTOR1_ref_dX=34 mm; CONNENCTOR1_ref1_02=49 mm; Hersteller=R. Nussbaum AG; Modell=55035.24; R. Nussbaum AG 55035.21 de Visibility=Nein; R. Nussbaum AG 55035.22 de Visibility=Nein; R. Nussbaum AG 55035.23 de Visibility=Nein; R. Nussbaum AG 55035.24 de Visibility=Ja; R. Nussbaum AG 55035.25 de Visibility=Nein; R. Nussbaum AG 55035.26 de Visibility=Nein; R. Nussbaum AG 55035.27 de Visibility=Nein; R. Nussbaum AG 55035.28 de Visibility=Nein; R. Nussbaum AG 55035.29 de Visibility=Nein; R. Nussbaum AG 55035.31 de Visibility=Nein; R. Nussbaum AG 55035.32 de Visibility=Nein; R. Nussbaum AG 55035.33 de Visibility=Nein; R. Nussbaum AG 55035.34 de Visibility=Nein; R. Nussbaum AG 55035.35 de Visibility=Nein; R. Nussbaum AG 55035.36 de Visibility=Nein; R. Nussbaum AG 55035.37 de Visibility=Nein; R. Nussbaum AG 55035.38 de Visibility=Nein; R. Nussbaum AG 55035.69 de Visibility=Nein; R. Nussbaum AG 55035.70 de Visibility=Nein; R. Nussbaum AG 55035.71 de Visibility=Nein; R. Nussbaum AG 55035.72 de Visibility=Nein; R. Nussbaum AG 55035.73 de Visibility=Nein; Typenkommentare=Optipress-Therm-Übergang DN=15x20

note: [stored X ft] marks values corroborated as IEEE doubles in the binary element streams (Revit-internal decimal feet)

## geometry (parser evidence)
native form markers: Sweep x3
no freeform markers — native parametric forms only
